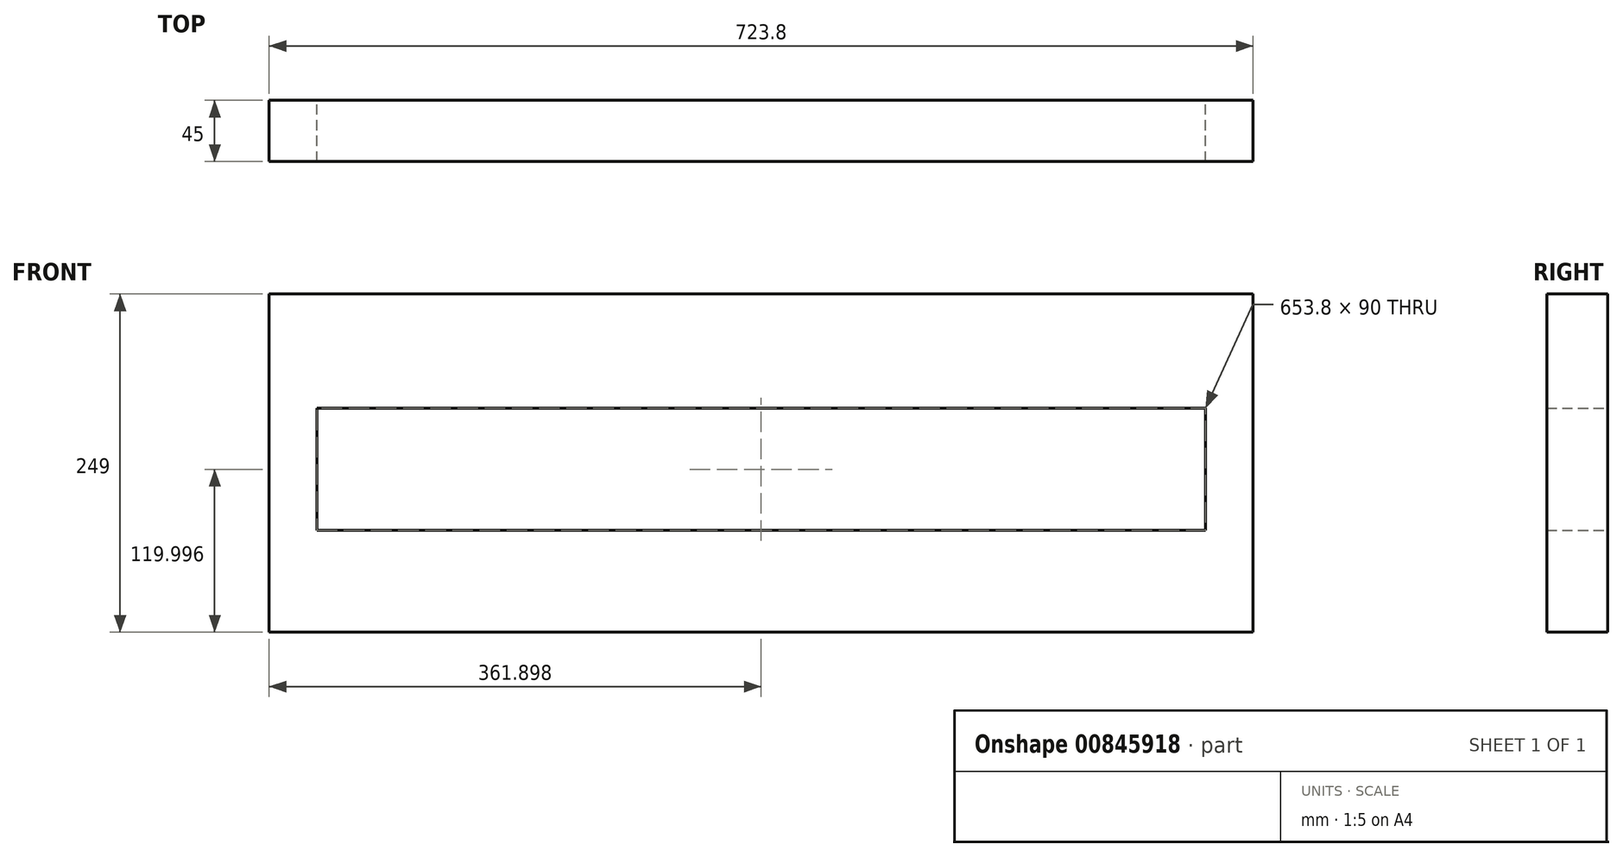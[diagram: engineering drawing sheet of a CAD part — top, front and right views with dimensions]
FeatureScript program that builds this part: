
annotation { "Feature Type Name" : "Feature", "Feature Type Description" : "" }
export const myFeature = defineFeature(function(context is Context, id is Id, definition is map)
    precondition{}
    {
        {
            var Q0;
            Q0=qCreatedBy(makeId("Front.planeOp"),FACE);
            var sketch = newSketch(context, id + "F0", { "sketchPlane" : qUnion([Q0])});
            skLineSegment(sketch, "E0", {"start": v(-291.08, -156.86) * mm, "end": v(432.72, -156.86) * mm});
            skLineSegment(sketch, "E1", {"start": v(432.72, -156.86) * mm, "end": v(432.72, 92.14) * mm});
            skLineSegment(sketch, "E2", {"start": v(432.72, 92.14) * mm, "end": v(-291.08, 92.14) * mm});
            skLineSegment(sketch, "E3", {"start": v(-291.08, 92.14) * mm, "end": v(-291.08, -156.86) * mm});
            skLineSegment(sketch, "E4", {"start": v(397.72, -81.86) * mm, "end": v(-256.08, -81.86) * mm});
            skLineSegment(sketch, "E5", {"start": v(-256.08, -81.86) * mm, "end": v(-256.08, 8.14) * mm});
            skLineSegment(sketch, "E6", {"start": v(-256.08, 8.14) * mm, "end": v(397.72, 8.14) * mm});
            skLineSegment(sketch, "E7", {"start": v(397.72, 8.14) * mm, "end": v(397.72, -81.86) * mm});
            skSolve(sketch);
        }
        {
            var Q0;
            Q0 = qSketchRegion(id + "F0", true);
            extrude(context, id + "F1", {"entities" : qUnion([Q0]), "depth" : 45 * mm, "offsetDistance" : 25 * mm});
        }
    });
